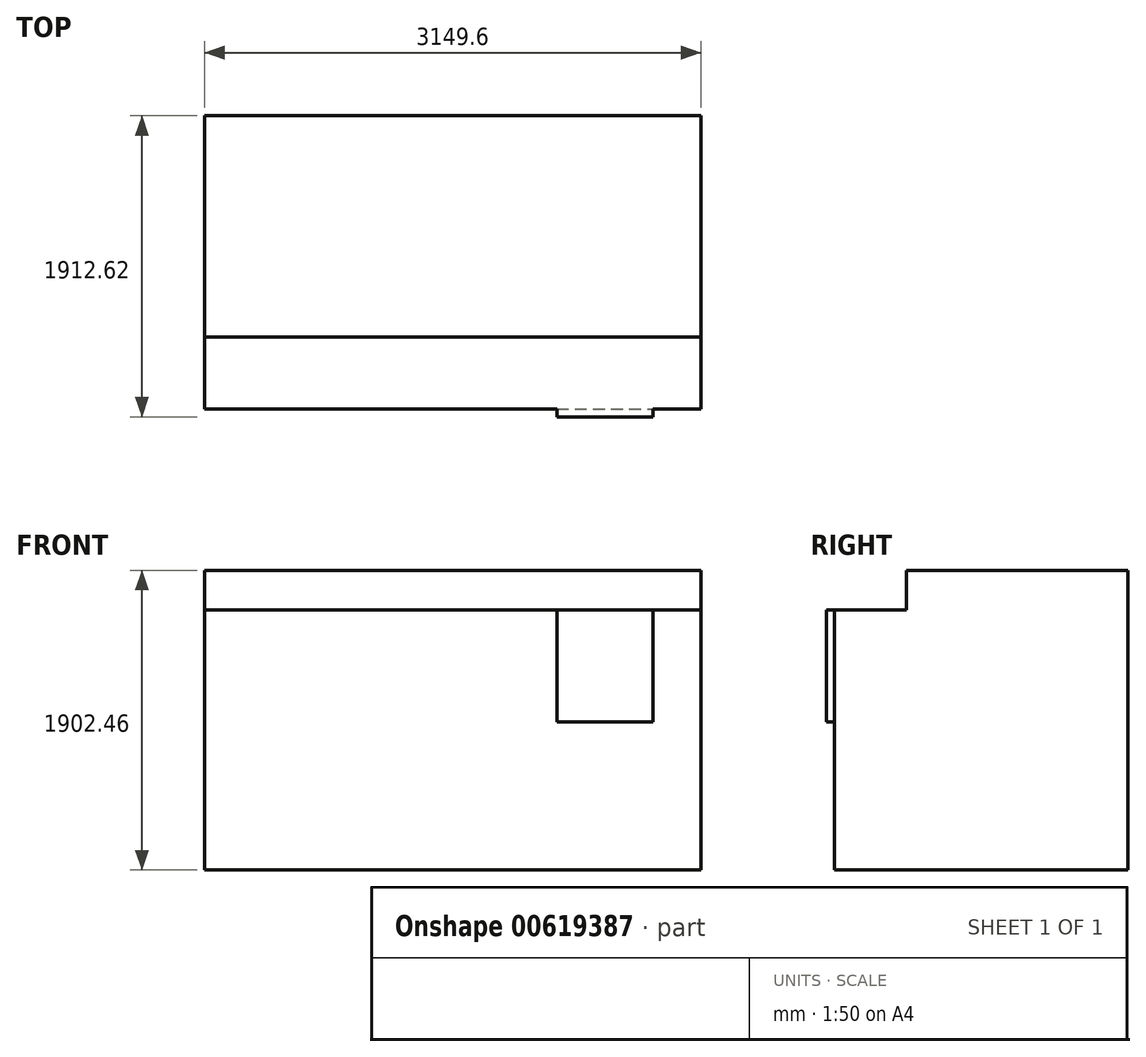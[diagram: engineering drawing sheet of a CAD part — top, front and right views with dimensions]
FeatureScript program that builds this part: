
annotation { "Feature Type Name" : "Feature", "Feature Type Description" : "" }
export const myFeature = defineFeature(function(context is Context, id is Id, definition is map)
    precondition{}
    {
        {
            var Q0;
            Q0=qCreatedBy(makeId("Right.planeOp"),FACE);
            var sketch = newSketch(context, id + "F0", { "sketchPlane" : qUnion([Q0])});
            skLineSegment(sketch, "E0", {"start": v(0, 0) * mm, "end": v(1861.82, 0) * mm});
            skLineSegment(sketch, "E1", {"start": v(1861.82, 0) * mm, "end": v(1861.82, 1902.46) * mm});
            skLineSegment(sketch, "E2", {"start": v(1861.82, 1902.46) * mm, "end": v(457.2, 1902.46) * mm});
            skLineSegment(sketch, "E3", {"start": v(457.2, 1902.46) * mm, "end": v(457.2, 1651) * mm});
            skLineSegment(sketch, "E4", {"start": v(457.2, 1651) * mm, "end": v(0, 1651) * mm});
            skLineSegment(sketch, "E5", {"start": v(0, 1651) * mm, "end": v(0, 0) * mm});
            skSolve(sketch);
        }
        {
            var Q0;
            Q0 = qSketchRegion(id + "F0", true);
            extrude(context, id + "F1", {"entities" : qUnion([Q0]), "endBound" : BoundingType.SYMMETRIC, "depth" : 3149.6 * mm, "offsetDistance" : 25.4 * mm});
        }
        {
            var Q0;
            Q0=makeQuery(id+"F1.opExtrude","SWEPT_FACE",FACE,{"disambiguationData":[OSD([sQuery(id+"F0.wireOp",EDGE,"E5")])]});
            var sketch = newSketch(context, id + "F2", { "sketchPlane" : qUnion([Q0])});
            skLineSegment(sketch, "E6.bottom", {"start": v(660.4, 1651) * mm, "end": v(1270, 1651) * mm});
            skLineSegment(sketch, "E6.top", {"start": v(660.4, 939.8) * mm, "end": v(1270, 939.8) * mm});
            skLineSegment(sketch, "E6.left", {"start": v(660.4, 1651) * mm, "end": v(660.4, 939.8) * mm});
            skLineSegment(sketch, "E6.right", {"start": v(1270, 1651) * mm, "end": v(1270, 939.8) * mm});
            skSolve(sketch);
        }
        {
            var Q0;
            Q0 = qSketchRegion(id + "F2", true);
            extrude(context, id + "F3", {"entities" : qUnion([Q0]), "operationType" : NewBodyOperationType.ADD, "depth" : 50.8 * mm, "offsetDistance" : 25.4 * mm});
        }
    });
